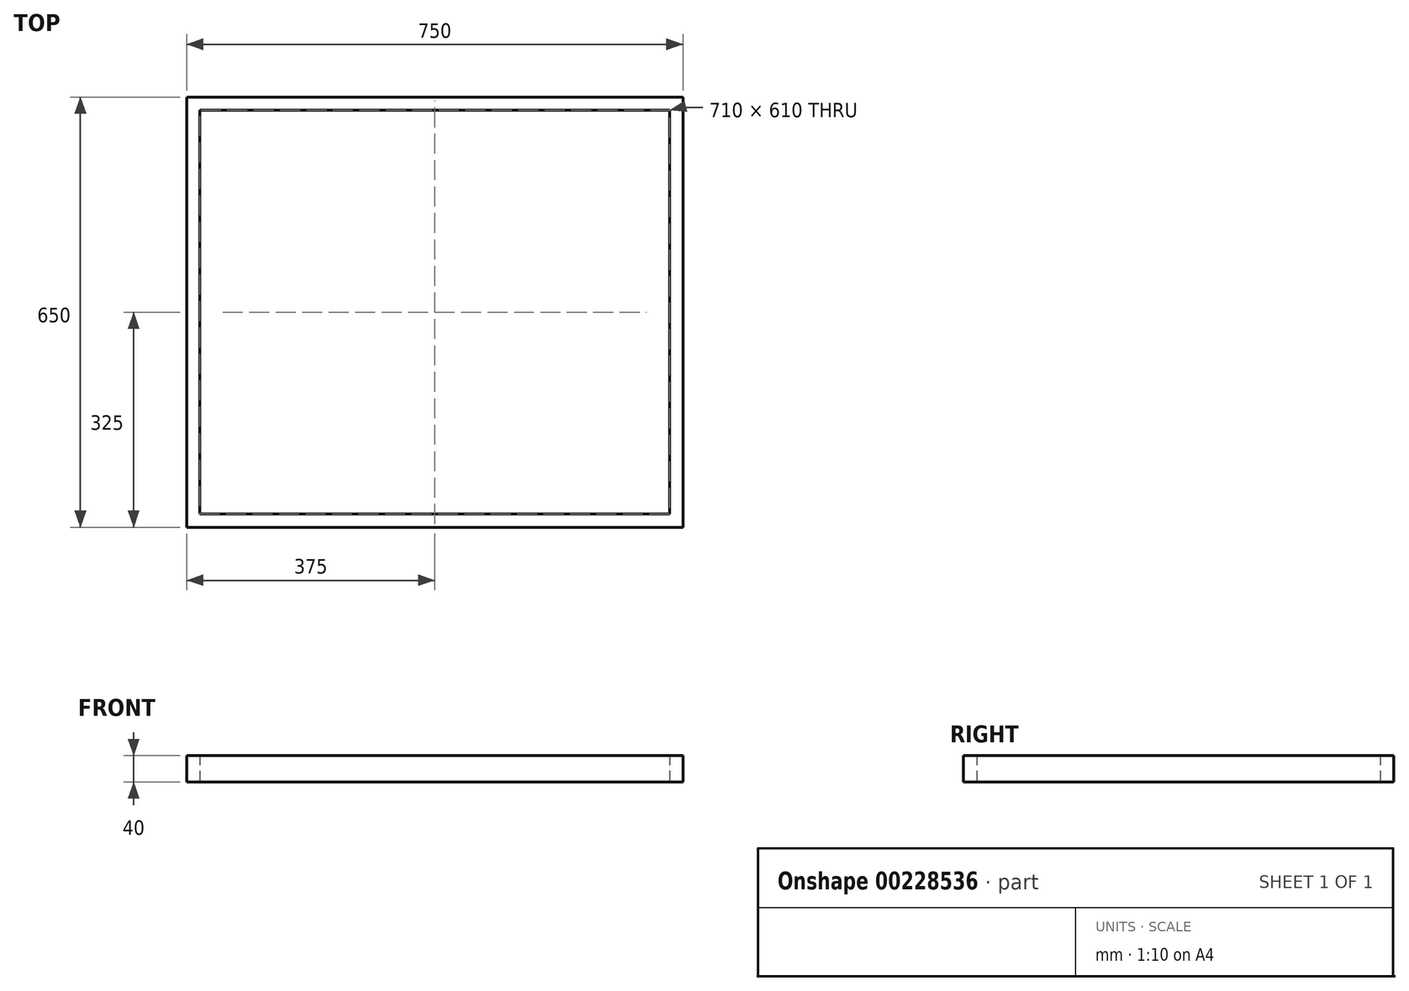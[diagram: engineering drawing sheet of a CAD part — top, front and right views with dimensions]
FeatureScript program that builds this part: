
annotation { "Feature Type Name" : "Feature", "Feature Type Description" : "" }
export const myFeature = defineFeature(function(context is Context, id is Id, definition is map)
    precondition{}
    {
        {
            var Q0;
            Q0=qCreatedBy(makeId("Top.planeOp"),FACE);
            var sketch = newSketch(context, id + "F0", { "sketchPlane" : qUnion([Q0])});
            skLineSegment(sketch, "E0.bottom", {"start": v(-375, 325) * mm, "end": v(375, 325) * mm});
            skLineSegment(sketch, "E0.top", {"start": v(-375, -325) * mm, "end": v(375, -325) * mm});
            skLineSegment(sketch, "E0.left", {"start": v(-375, 325) * mm, "end": v(-375, -325) * mm});
            skLineSegment(sketch, "E0.right", {"start": v(375, 325) * mm, "end": v(375, -325) * mm});
            skPoint(sketch, "E0.middle", {"position": v(0, 0) * mm});
            skLineSegment(sketch, "E1.bottom", {"start": v(355, 305) * mm, "end": v(-355, 305) * mm});
            skLineSegment(sketch, "E1.top", {"start": v(355, -305) * mm, "end": v(-355, -305) * mm});
            skLineSegment(sketch, "E1.left", {"start": v(355, 305) * mm, "end": v(355, -305) * mm});
            skLineSegment(sketch, "E1.right", {"start": v(-355, 305) * mm, "end": v(-355, -305) * mm});
            skSolve(sketch);
        }
        {
            var Q0;
            Q0=makeQuery(id+"F0.imprint","IMPRINT",FACE,{"disambiguationData":[TD([[makeQuery(id+"F0.imprint","IMPRINT",EDGE,{"derivedFrom":sQuery(id+"F0.wireOp",EDGE,"E0.bottom")}),-1.0]])]});
            extrude(context, id + "F1", {"entities" : qUnion([Q0]), "depth" : 40 * mm});
        }
    });
